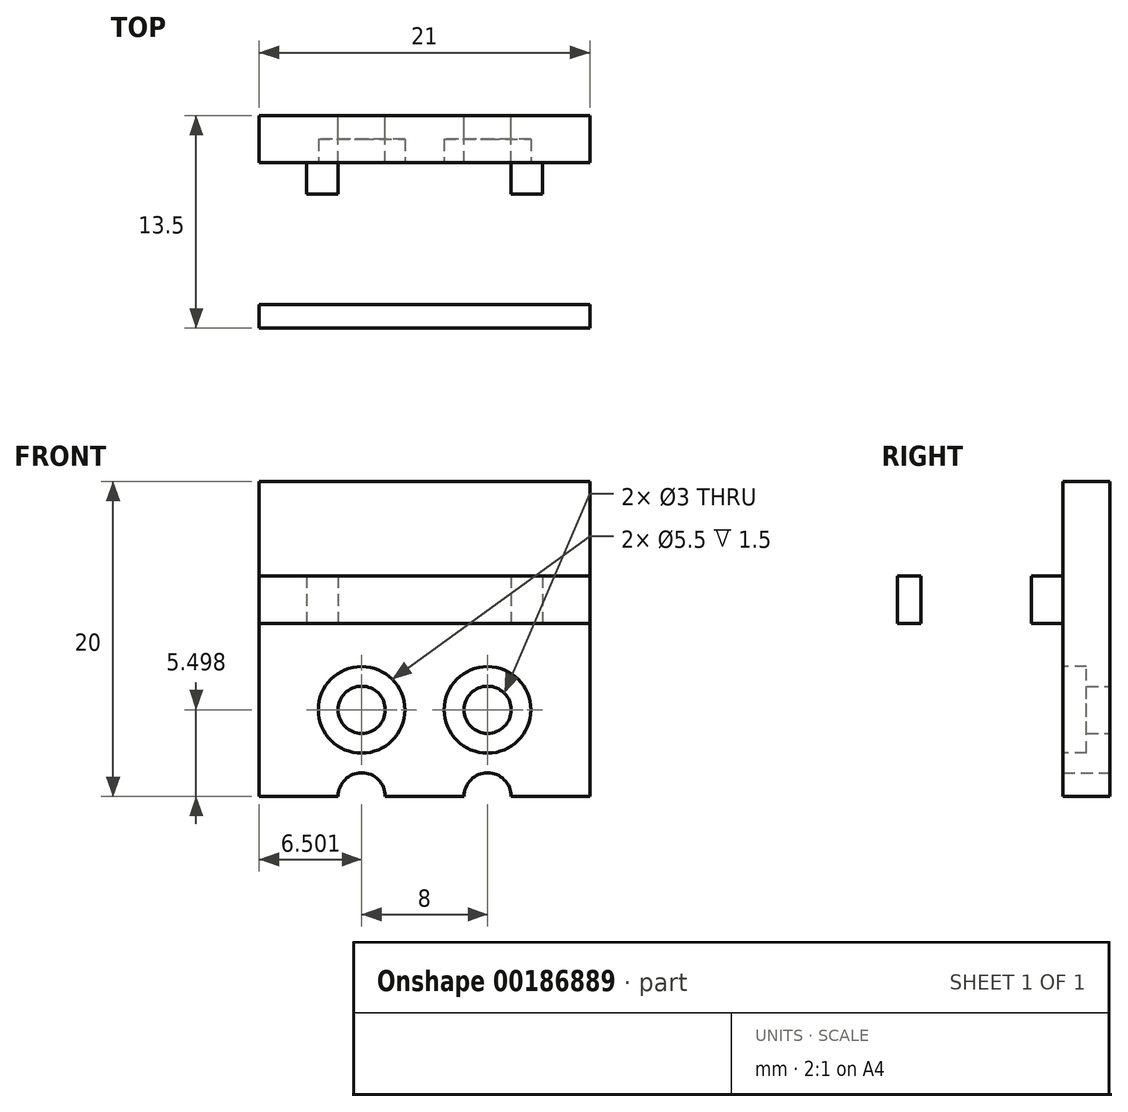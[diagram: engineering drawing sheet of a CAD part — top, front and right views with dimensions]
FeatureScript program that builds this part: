
annotation { "Feature Type Name" : "Feature", "Feature Type Description" : "" }
export const myFeature = defineFeature(function(context is Context, id is Id, definition is map)
    precondition{}
    {
        {
            var Q0;
            Q0=qCreatedBy(makeId("Front.planeOp"),FACE);
            var sketch = newSketch(context, id + "F4", { "sketchPlane" : qUnion([Q0])});
            skLineSegment(sketch, "E0", {"start": v(-3.88, 25.17) * mm, "end": v(1.12, 25.17) * mm});
            skCircle(sketch, "E1", {"center": v(-5.38, 25.17) * mm, "radius": 1.5 * mm});
            skCircle(sketch, "E2", {"center": v(2.62, 25.17) * mm, "radius": 1.5 * mm});
            skLineSegment(sketch, "E3.bottom", {"start": v(9.12, 19.67) * mm, "end": v(-11.88, 19.67) * mm});
            skLineSegment(sketch, "E3.top", {"start": v(9.12, 30.67) * mm, "end": v(-11.88, 30.67) * mm});
            skLineSegment(sketch, "E3.left", {"start": v(9.12, 19.67) * mm, "end": v(9.12, 30.67) * mm});
            skLineSegment(sketch, "E3.right", {"start": v(-11.88, 19.67) * mm, "end": v(-11.88, 30.67) * mm});
            skPoint(sketch, "E3.middle", {"position": v(-1.38, 25.17) * mm});
            skLineSegment(sketch, "E4", {"start": v(-5.38, 25.17) * mm, "end": v(-5.38, 19.67) * mm});
            skLineSegment(sketch, "E5", {"start": v(2.62, 19.67) * mm, "end": v(2.62, 25.17) * mm});
            skCircle(sketch, "E6", {"center": v(-5.38, 19.67) * mm, "radius": 1.5 * mm});
            skCircle(sketch, "E7", {"center": v(2.62, 19.67) * mm, "radius": 1.5 * mm});
            skSolve(sketch);
        }
        {
            var Q0;
            {var subQ15=sQuery(id+"F4.wireOp",EDGE,"E0");Q0=makeQuery(id+"F4.imprint","IMPRINT",FACE,{"disambiguationData":[TD([[makeQuery(id+"F4.imprint","IMPRINT",EDGE,{"derivedFrom":subQ15}),1.0]])]});}
            var Q1;
            {var subQ6=sQuery(id+"F4.wireOp",EDGE,"E0");Q1=makeQuery(id+"F4.imprint","IMPRINT",FACE,{"disambiguationData":[TD([[makeQuery(id+"F4.imprint","IMPRINT",EDGE,{"derivedFrom":subQ6}),-1.0]])]});}
            extrude(context, id + "F0", {"entities" : qUnion([Q0, Q1]), "depth" : 3 * mm});
        }
        {
            var Q0;
            Q0=makeQuery(id+"F0.opExtrude","SWEPT_FACE",FACE,{"disambiguationData":[OSD([sQuery(id+"F4.wireOp",EDGE,"E3.top")])]});
            var sketch = newSketch(context, id + "F1", { "sketchPlane" : qUnion([Q0])});
            skLineSegment(sketch, "E8.bottom", {"start": v(-11.88, 0) * mm, "end": v(9.12, 0) * mm});
            skLineSegment(sketch, "E8.top", {"start": v(-11.88, -15) * mm, "end": v(9.12, -15) * mm});
            skLineSegment(sketch, "E8.left", {"start": v(-11.88, 0) * mm, "end": v(-11.88, -15) * mm});
            skLineSegment(sketch, "E8.right", {"start": v(9.12, 0) * mm, "end": v(9.12, -15) * mm});
            skLineSegment(sketch, "E9.bottom", {"start": v(9.12, -3) * mm, "end": v(-11.88, -3) * mm});
            skLineSegment(sketch, "E9.top", {"start": v(9.12, 0) * mm, "end": v(-11.88, 0) * mm});
            skLineSegment(sketch, "E9.left", {"start": v(9.12, -3) * mm, "end": v(9.12, 0) * mm});
            skLineSegment(sketch, "E9.right", {"start": v(-11.88, -3) * mm, "end": v(-11.88, 0) * mm});
            skLineSegment(sketch, "E10.top", {"start": v(-11.88, -12) * mm, "end": v(9.12, -12) * mm});
            skLineSegment(sketch, "E10.left", {"start": v(-11.88, -15) * mm, "end": v(-11.88, -12) * mm});
            skLineSegment(sketch, "E10.right", {"start": v(9.12, -15) * mm, "end": v(9.12, -12) * mm});
            skLineSegment(sketch, "E11.bottom", {"start": v(-11.88, -3) * mm, "end": v(-8.88, -3) * mm});
            skLineSegment(sketch, "E11.top", {"start": v(-11.88, -12) * mm, "end": v(-8.88, -12) * mm});
            skLineSegment(sketch, "E11.left", {"start": v(-11.88, -3) * mm, "end": v(-11.88, -12) * mm});
            skLineSegment(sketch, "E11.right", {"start": v(-8.88, -3) * mm, "end": v(-8.88, -12) * mm});
            skLineSegment(sketch, "E12.bottom", {"start": v(9.12, -3) * mm, "end": v(6.12, -3) * mm});
            skLineSegment(sketch, "E12.top", {"start": v(9.12, -12) * mm, "end": v(6.12, -12) * mm});
            skLineSegment(sketch, "E12.left", {"start": v(9.12, -3) * mm, "end": v(9.12, -12) * mm});
            skLineSegment(sketch, "E12.right", {"start": v(6.12, -3) * mm, "end": v(6.12, -12) * mm});
            skLineSegment(sketch, "E13", {"start": v(-8.88, -7.5) * mm, "end": v(-1.38, -7.5) * mm, "construction": true});
            skPoint(sketch, "E13.endSnap0", {"position": v(-8.88, -7.5) * mm});
            skLineSegment(sketch, "E14.bottom", {"start": v(2.12, -6.5) * mm, "end": v(-4.88, -6.5) * mm});
            skLineSegment(sketch, "E14.top", {"start": v(2.12, -8.5) * mm, "end": v(-4.88, -8.5) * mm});
            skLineSegment(sketch, "E14.left", {"start": v(2.12, -6.5) * mm, "end": v(2.12, -8.5) * mm});
            skLineSegment(sketch, "E14.right", {"start": v(-4.88, -6.5) * mm, "end": v(-4.88, -8.5) * mm});
            skPoint(sketch, "E14.middle", {"position": v(-1.38, -7.5) * mm});
            skLineSegment(sketch, "E15", {"start": v(-11.88, -13.5) * mm, "end": v(9.12, -13.5) * mm});
            skPoint(sketch, "E16.top.end.orphan", {"position": v(4.62, -10.5) * mm});
            skPoint(sketch, "E16.left.end.orphan", {"position": v(6.12, -10.5) * mm});
            skPoint(sketch, "E16.bottom.end.orphan", {"position": v(4.62, -12) * mm});
            skLineSegment(sketch, "E17.top", {"start": v(4.62, -12) * mm, "end": v(6.12, -12) * mm});
            skLineSegment(sketch, "E18.bottom", {"start": v(-8.88, -3) * mm, "end": v(-6.88, -3) * mm});
            skLineSegment(sketch, "E18.top", {"start": v(-8.88, -5) * mm, "end": v(-6.88, -5) * mm});
            skLineSegment(sketch, "E18.left", {"start": v(-8.88, -3) * mm, "end": v(-8.88, -5) * mm});
            skLineSegment(sketch, "E18.right", {"start": v(-6.88, -3) * mm, "end": v(-6.88, -5) * mm});
            skLineSegment(sketch, "E19.bottom", {"start": v(6.12, -3) * mm, "end": v(4.12, -3) * mm});
            skLineSegment(sketch, "E19.top", {"start": v(6.12, -5) * mm, "end": v(4.12, -5) * mm});
            skLineSegment(sketch, "E19.left", {"start": v(6.12, -3) * mm, "end": v(6.12, -5) * mm});
            skLineSegment(sketch, "E19.right", {"start": v(4.12, -3) * mm, "end": v(4.12, -5) * mm});
            skLineSegment(sketch, "E20", {"start": v(4.12, -5) * mm, "end": v(4.12, -9.5) * mm, "construction": true});
            skLineSegment(sketch, "E21.bottom", {"start": v(4.12, -9.5) * mm, "end": v(6.12, -9.5) * mm});
            skLineSegment(sketch, "E21.top", {"start": v(4.12, -11.5) * mm, "end": v(6.12, -11.5) * mm});
            skLineSegment(sketch, "E21.left", {"start": v(4.12, -9.5) * mm, "end": v(4.12, -11.5) * mm});
            skLineSegment(sketch, "E21.right", {"start": v(6.12, -9.5) * mm, "end": v(6.12, -11.5) * mm});
            skLineSegment(sketch, "E22", {"start": v(-6.88, -5) * mm, "end": v(-6.88, -9.5) * mm, "construction": true});
            skLineSegment(sketch, "E23.bottom", {"start": v(-6.88, -9.5) * mm, "end": v(-8.88, -9.5) * mm});
            skLineSegment(sketch, "E23.top", {"start": v(-6.88, -11.5) * mm, "end": v(-8.88, -11.5) * mm});
            skLineSegment(sketch, "E23.left", {"start": v(-6.88, -9.5) * mm, "end": v(-6.88, -11.5) * mm});
            skLineSegment(sketch, "E23.right", {"start": v(-8.88, -9.5) * mm, "end": v(-8.88, -11.5) * mm});
            skSolve(sketch);
        }
        {
            var Q0;
            Q0=makeQuery(id+"F1.imprint","IMPRINT",FACE,{"disambiguationData":[TD([[makeQuery(id+"F1.imprint","IMPRINT",EDGE,{"derivedFrom":sQuery(id+"F1.wireOp",EDGE,"E9.bottom")}),-1.0]])]});
            var Q1;
            Q1=makeQuery(id+"F1.imprint","IMPRINT",FACE,{"disambiguationData":[TD([[makeQuery(id+"F1.imprint","IMPRINT",EDGE,{"derivedFrom":sQuery(id+"F1.wireOp",EDGE,"E11.bottom")}),1.0]])]});
            var Q2;
            Q2=makeQuery(id+"F1.imprint","IMPRINT",FACE,{"disambiguationData":[TD([[makeQuery(id+"F1.imprint","IMPRINT",EDGE,{"derivedFrom":sQuery(id+"F1.wireOp",EDGE,"E12.bottom")}),1.0]])]});
            extrude(context, id + "F5", {"entities" : qUnion([Q0, Q1, Q2]), "operationType" : NewBodyOperationType.ADD, "depth" : 9 * mm});
        }
        {
            var Q0;
            Q0=makeQuery(id+"F1.imprint","IMPRINT",FACE,{"disambiguationData":[TD([[makeQuery(id+"F1.imprint","IMPRINT",EDGE,{"derivedFrom":sQuery(id+"F1.wireOp",EDGE,"E9.bottom")}),1.0]])]});
            var Q1;
            Q1=makeQuery(id+"F1.imprint","IMPRINT",FACE,{"disambiguationData":[TD([[makeQuery(id+"F1.imprint","IMPRINT",EDGE,{"derivedFrom":sQuery(id+"F1.wireOp",EDGE,"E10.top")}),-1.0]])]});
            extrude(context, id + "F6", {"entities" : qUnion([Q0, Q1]), "operationType" : NewBodyOperationType.ADD, "depth" : 3 * mm});
        }
        {
            var Q0;
            Q0=makeQuery(id+"F5.boolean.opBoolean","MERGE",FACE,{"derivedFrom":[makeQuery(id+"F0.opExtrude","CAP_FACE",FACE,{"disambiguationData":[OSD([sQuery(id+"F4.wireOp",EDGE,"E1"),sQuery(id+"F4.wireOp",EDGE,"E2"),sQuery(id+"F4.wireOp",EDGE,"E3.bottom"),sQuery(id+"F4.wireOp",EDGE,"E3.top"),sQuery(id+"F4.wireOp",EDGE,"E3.left"),sQuery(id+"F4.wireOp",EDGE,"E3.right"),sQuery(id+"F4.wireOp",EDGE,"E6"),sQuery(id+"F4.wireOp",EDGE,"E7")])],"isStart":false}),makeQuery(id+"F5.opExtrude","SWEPT_FACE",FACE,{"disambiguationData":[OSD([sQuery(id+"F1.wireOp",EDGE,"E9.bottom"),sQuery(id+"F1.wireOp",EDGE,"E18.bottom"),sQuery(id+"F1.wireOp",EDGE,"E19.bottom")])]})]});
            var sketch = newSketch(context, id + "F2", { "sketchPlane" : qUnion([Q0])});
            skCircle(sketch, "E24", {"center": v(-5.38, 25.17) * mm, "radius": 2.75 * mm});
            skCircle(sketch, "E25", {"center": v(2.62, 25.17) * mm, "radius": 2.75 * mm});
            skSolve(sketch);
        }
        {
            var Q0;
            Q0=makeQuery(id+"F2.imprint","IMPRINT",FACE,{"disambiguationData":[TD([[makeQuery(id+"F2.imprint","IMPRINT",EDGE,{"derivedFrom":sQuery(id+"F2.wireOp",EDGE,"E25")}),1.0]])]});
            var Q1;
            Q1=makeQuery(id+"F2.imprint","IMPRINT",FACE,{"disambiguationData":[TD([[makeQuery(id+"F2.imprint","IMPRINT",EDGE,{"derivedFrom":sQuery(id+"F2.wireOp",EDGE,"E24")}),1.0]])]});
            extrude(context, id + "F3", {"entities" : qUnion([Q0, Q1]), "operationType" : NewBodyOperationType.REMOVE, "oppositeDirection" : true, "depth" : 1.5 * mm});
        }
    });
